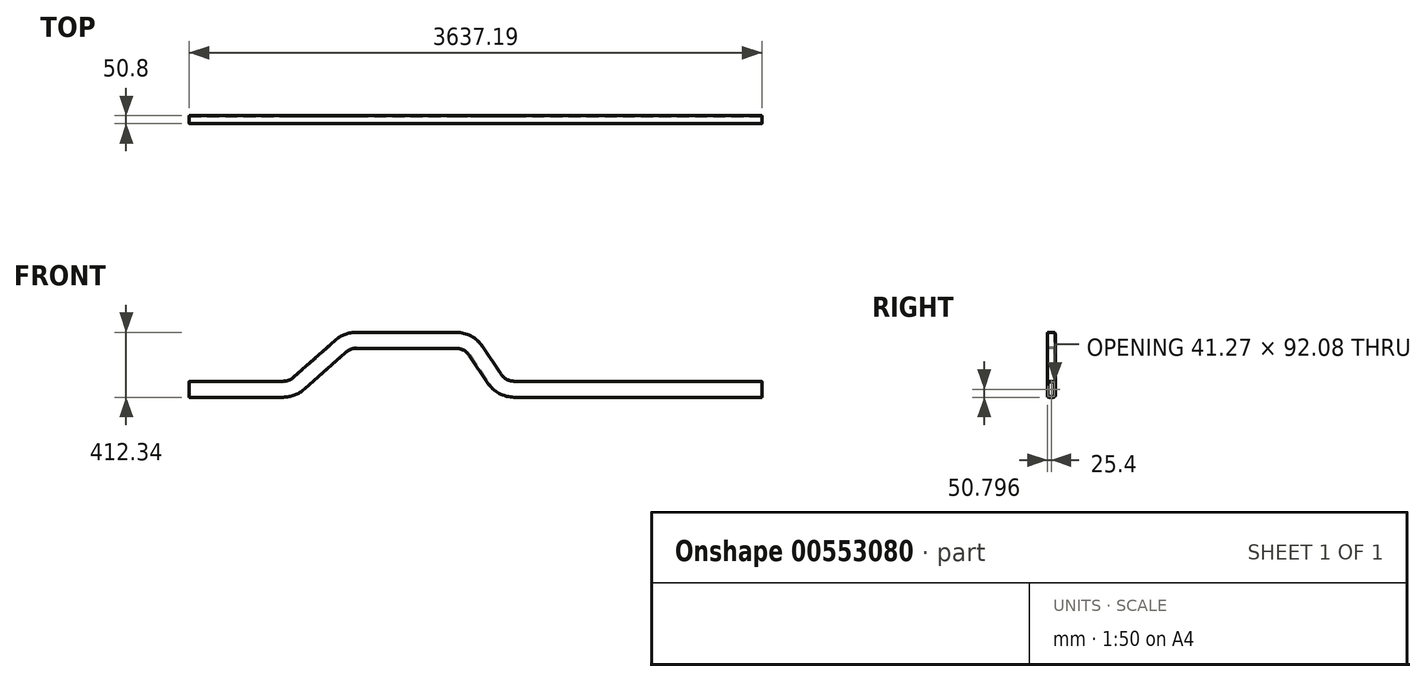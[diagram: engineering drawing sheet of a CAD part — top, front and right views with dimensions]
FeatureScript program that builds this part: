
annotation { "Feature Type Name" : "Feature", "Feature Type Description" : "" }
export const myFeature = defineFeature(function(context is Context, id is Id, definition is map)
    precondition{}
    {
        {
            var Q0;
            Q0=qCreatedBy(makeId("Front.planeOp"),FACE);
            var sketch = newSketch(context, id + "F0", { "sketchPlane" : qUnion([Q0])});
            skLineSegment(sketch, "E0", {"start": v(-434.45, -46) * mm, "end": v(161.56, -46) * mm});
            skLineSegment(sketch, "E1", {"start": v(262.8, -7.52) * mm, "end": v(525.85, 226.26) * mm});
            skLineSegment(sketch, "E2", {"start": v(627.09, 264.74) * mm, "end": v(1259.54, 264.74) * mm});
            skLineSegment(sketch, "E3", {"start": v(1386.31, 196.92) * mm, "end": v(1503.13, 21.82) * mm});
            skLineSegment(sketch, "E4", {"start": v(1629.9, -46) * mm, "end": v(3202.74, -46) * mm});
            skPoint(sketch, "E5.visualSharp", {"position": v(219.49, -46) * mm});
            skArc(sketch, "E5.filletArc", {"start": v(161.56, -46) * mm, "mid": v(215.7, -36.06) * mm, "end": v(262.8, -7.52) * mm});
            skPoint(sketch, "E6.visualSharp", {"position": v(569.16, 264.74) * mm});
            skArc(sketch, "E6.filletArc", {"start": v(627.09, 264.74) * mm, "mid": v(572.94, 254.8) * mm, "end": v(525.85, 226.26) * mm});
            skPoint(sketch, "E7.visualSharp", {"position": v(1341.07, 264.74) * mm});
            skArc(sketch, "E7.filletArc", {"start": v(1386.31, 196.92) * mm, "mid": v(1331.43, 246.72) * mm, "end": v(1259.54, 264.74) * mm});
            skPoint(sketch, "E8.visualSharp", {"position": v(1548.37, -46) * mm});
            skArc(sketch, "E8.filletArc", {"start": v(1503.13, 21.82) * mm, "mid": v(1558.01, -27.98) * mm, "end": v(1629.9, -46) * mm});
            skSolve(sketch);
        }
        {
            var Q0;
            Q0=sQuery(id+"F0.wireOp",VERTEX,"E0.start");
            var Q1;
            Q1=sQuery(id+"F0.wireOp",EDGE,"E0");
            cPlane(context, id + "F1", {"entities" : qUnion([Q0, Q1]), "cplaneType" : CPlaneType.LINE_POINT, "offset" : 25.4 * mm, "width" : 152.4 * mm, "height" : 152.4 * mm});
        }
        {
            var Q0;
            Q0=qCreatedBy(id+"F1.planeOp",FACE);
            var sketch = newSketch(context, id + "F2", { "sketchPlane" : qUnion([Q0])});
            skLineSegment(sketch, "E9.bottom", {"start": v(15.87, 4.8) * mm, "end": v(-15.88, 4.8) * mm});
            skLineSegment(sketch, "E9.top", {"start": v(15.88, -96.8) * mm, "end": v(-15.87, -96.8) * mm});
            skLineSegment(sketch, "E9.left", {"start": v(25.4, -4.73) * mm, "end": v(25.4, -87.28) * mm});
            skLineSegment(sketch, "E9.right", {"start": v(-25.4, -4.73) * mm, "end": v(-25.4, -87.28) * mm});
            skPoint(sketch, "E9.middle", {"position": v(0, -46) * mm});
            skPoint(sketch, "E10.visualSharp", {"position": v(25.4, 4.8) * mm});
            skArc(sketch, "E10.filletArc", {"start": v(25.4, -4.73) * mm, "mid": v(22.61, 2) * mm, "end": v(15.87, 4.8) * mm});
            skPoint(sketch, "E11.visualSharp", {"position": v(-25.4, 4.8) * mm});
            skArc(sketch, "E11.filletArc", {"start": v(-15.88, 4.8) * mm, "mid": v(-22.61, 2) * mm, "end": v(-25.4, -4.73) * mm});
            skPoint(sketch, "E12.visualSharp", {"position": v(-25.4, -96.8) * mm});
            skArc(sketch, "E12.filletArc", {"start": v(-25.4, -87.28) * mm, "mid": v(-22.61, -94.01) * mm, "end": v(-15.87, -96.8) * mm});
            skPoint(sketch, "E13.visualSharp", {"position": v(25.4, -96.8) * mm});
            skArc(sketch, "E13.filletArc", {"start": v(15.88, -96.8) * mm, "mid": v(22.61, -94.01) * mm, "end": v(25.4, -87.28) * mm});
            skArc(sketch, "E14.0", {"start": v(20.64, -4.73) * mm, "mid": v(19.24, -1.36) * mm, "end": v(15.87, 0.03) * mm});
            skLineSegment(sketch, "E14.1", {"start": v(20.64, -4.73) * mm, "end": v(20.64, -87.28) * mm});
            skLineSegment(sketch, "E14.2", {"start": v(15.87, 0.03) * mm, "end": v(-15.88, 0.03) * mm});
            skArc(sketch, "E14.3", {"start": v(15.88, -92.04) * mm, "mid": v(19.24, -90.65) * mm, "end": v(20.64, -87.28) * mm});
            skArc(sketch, "E14.4", {"start": v(-15.88, 0.03) * mm, "mid": v(-19.24, -1.36) * mm, "end": v(-20.64, -4.73) * mm});
            skLineSegment(sketch, "E14.5", {"start": v(-20.64, -4.73) * mm, "end": v(-20.64, -87.28) * mm});
            skArc(sketch, "E14.6", {"start": v(-20.64, -87.28) * mm, "mid": v(-19.24, -90.65) * mm, "end": v(-15.87, -92.04) * mm});
            skLineSegment(sketch, "E14.7", {"start": v(15.88, -92.04) * mm, "end": v(-15.87, -92.04) * mm});
            skSolve(sketch);
        }
        {
            var Q0;
            Q0 = qSketchRegion(id + "F2", true);
            var Q1;
            Q1=sQuery(id+"F0.wireOp",EDGE,"E4");
            var Q2;
            Q2=sQuery(id+"F0.wireOp",EDGE,"E8.filletArc");
            var Q3;
            Q3=sQuery(id+"F0.wireOp",EDGE,"E3");
            var Q4;
            Q4=sQuery(id+"F0.wireOp",EDGE,"E7.filletArc");
            var Q5;
            Q5=sQuery(id+"F0.wireOp",EDGE,"E2");
            var Q6;
            Q6=sQuery(id+"F0.wireOp",EDGE,"E6.filletArc");
            var Q7;
            Q7=sQuery(id+"F0.wireOp",EDGE,"E1");
            var Q8;
            Q8=sQuery(id+"F0.wireOp",EDGE,"E5.filletArc");
            var Q9;
            Q9=sQuery(id+"F0.wireOp",EDGE,"E0");
            sweep(context, id + "F3", {"profiles" : qUnion([Q0]), "path" : qUnion([Q1, Q2, Q3, Q4, Q5, Q6, Q7, Q8, Q9])});
        }
    });
